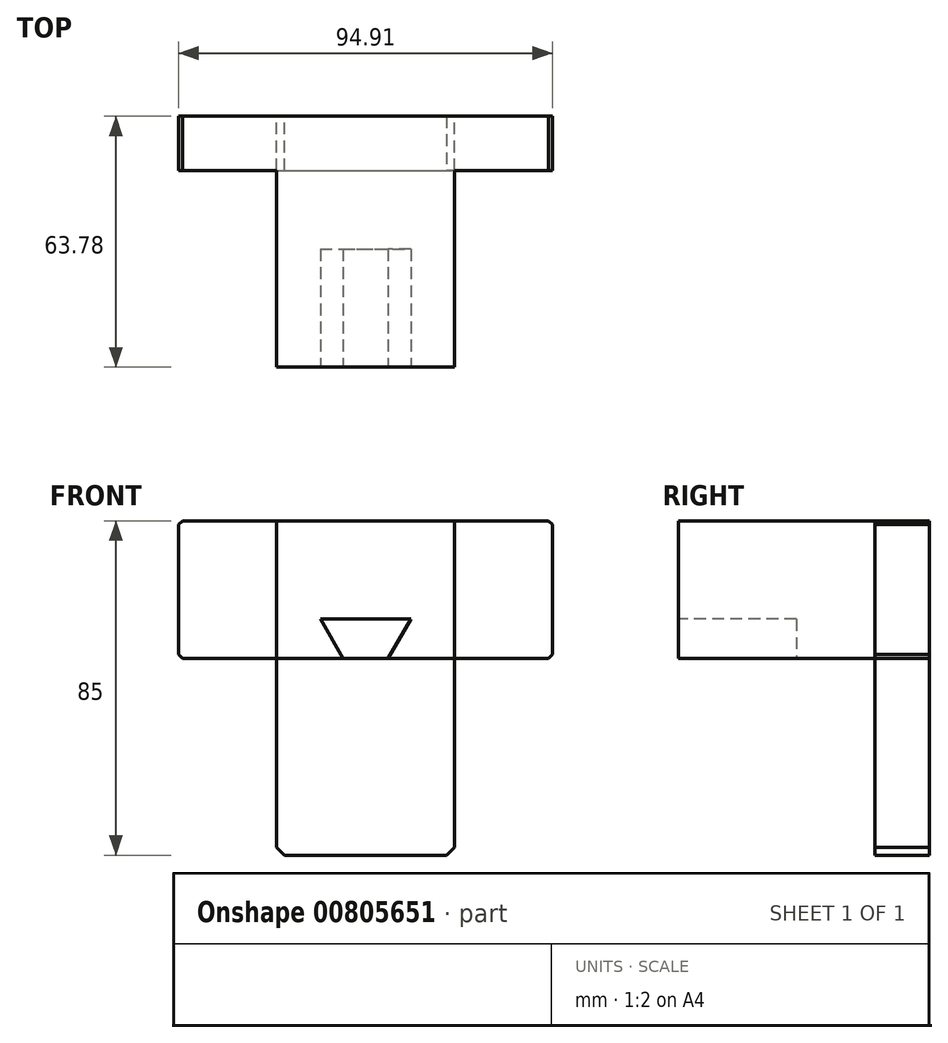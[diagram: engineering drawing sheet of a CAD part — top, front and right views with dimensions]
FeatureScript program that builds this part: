
annotation { "Feature Type Name" : "Feature", "Feature Type Description" : "" }
export const myFeature = defineFeature(function(context is Context, id is Id, definition is map)
    precondition{}
    {
        {
            var Q0;
            Q0=qCreatedBy(makeId("Front.planeOp"),FACE);
            var sketch = newSketch(context, id + "F0", { "sketchPlane" : qUnion([Q0])});
            skLineSegment(sketch, "E0.bottom", {"start": v(-47.93, 7.07) * mm, "end": v(46.98, 7.07) * mm});
            skLineSegment(sketch, "E0.top", {"start": v(-47.93, -27.93) * mm, "end": v(46.98, -27.93) * mm});
            skLineSegment(sketch, "E0.left", {"start": v(-47.93, 7.07) * mm, "end": v(-47.93, -27.93) * mm});
            skLineSegment(sketch, "E0.right", {"start": v(46.98, 7.07) * mm, "end": v(46.98, -27.93) * mm});
            skSolve(sketch);
        }
        {
            var Q0;
            Q0=makeQuery(id+"F0.imprint","IMPRINT",FACE,{"disambiguationData":[TD([[makeQuery(id+"F0.imprint","IMPRINT",EDGE,{"derivedFrom":sQuery(id+"F0.wireOp",EDGE,"E0.bottom")}),-1.0]])]});
            extrude(context, id + "F1", {"entities" : qUnion([Q0]), "depth" : 13.78 * mm, "offsetDistance" : 25 * mm});
        }
        {
            var Q0;
            Q0=makeQuery(id+"F1.opExtrude","SWEPT_EDGE",EDGE,{"disambiguationData":[OSD([sQuery(id+"F0.wireOp",EDGE,"E0.top"),sQuery(id+"F0.wireOp",EDGE,"E0.left")])]});
            var Q1;
            Q1=makeQuery(id+"F1.opExtrude","SWEPT_EDGE",EDGE,{"disambiguationData":[OSD([sQuery(id+"F0.wireOp",EDGE,"E0.top"),sQuery(id+"F0.wireOp",EDGE,"E0.right")])]});
            var Q2;
            Q2=makeQuery(id+"F1.opExtrude","SWEPT_EDGE",EDGE,{"disambiguationData":[OSD([sQuery(id+"F0.wireOp",EDGE,"E0.bottom"),sQuery(id+"F0.wireOp",EDGE,"E0.right")])]});
            var Q3;
            Q3=makeQuery(id+"F1.opExtrude","SWEPT_EDGE",EDGE,{"disambiguationData":[OSD([sQuery(id+"F0.wireOp",EDGE,"E0.bottom"),sQuery(id+"F0.wireOp",EDGE,"E0.left")])]});
            chamfer(context, id + "F2", {"entities" : qUnion([Q0, Q1, Q2, Q3]), "width" : 1 * mm, "tangentPropagation" : true});
        }
        {
            var Q0;
            Q0=makeQuery(id+"F1.opExtrude","CAP_FACE",FACE,{"disambiguationData":[OSD([sQuery(id+"F0.wireOp",EDGE,"E0.bottom"),sQuery(id+"F0.wireOp",EDGE,"E0.top"),sQuery(id+"F0.wireOp",EDGE,"E0.left"),sQuery(id+"F0.wireOp",EDGE,"E0.right")])],"isStart":false});
            var sketch = newSketch(context, id + "F3", { "sketchPlane" : qUnion([Q0])});
            skLineSegment(sketch, "E1.bottom", {"start": v(-23.06, 7.07) * mm, "end": v(22.1, 7.07) * mm});
            skLineSegment(sketch, "E1.top", {"start": v(-23.06, -27.93) * mm, "end": v(22.1, -27.93) * mm});
            skLineSegment(sketch, "E1.left", {"start": v(-23.06, 7.07) * mm, "end": v(-23.06, -27.93) * mm});
            skLineSegment(sketch, "E1.right", {"start": v(22.1, 7.07) * mm, "end": v(22.1, -27.93) * mm});
            skSolve(sketch);
        }
        {
            var Q0;
            Q0=makeQuery(id+"F3.imprint","IMPRINT",FACE,{"disambiguationData":[TD([[makeQuery(id+"F3.imprint","IMPRINT",EDGE,{"derivedFrom":sQuery(id+"F3.wireOp",EDGE,"E1.bottom")}),-1.0]])]});
            extrude(context, id + "F4", {"entities" : qUnion([Q0]), "operationType" : NewBodyOperationType.ADD, "depth" : 50 * mm, "offsetDistance" : 25 * mm});
        }
        {
            var Q0;
            Q0=makeQuery(id+"F4.boolean.opBoolean","MERGE",FACE,{"derivedFrom":[makeQuery(id+"F1.opExtrude","SWEPT_FACE",FACE,{"disambiguationData":[OSD([sQuery(id+"F0.wireOp",EDGE,"E0.top")])]}),makeQuery(id+"F4.opExtrude","SWEPT_FACE",FACE,{"disambiguationData":[OSD([sQuery(id+"F3.wireOp",EDGE,"E1.top")])]})]});
            var sketch = newSketch(context, id + "F5", { "sketchPlane" : qUnion([Q0])});
            skLineSegment(sketch, "E2.bottom", {"start": v(-23.06, 13.78) * mm, "end": v(22.1, 13.78) * mm});
            skLineSegment(sketch, "E2.top", {"start": v(-23.06, 0) * mm, "end": v(22.1, 0) * mm});
            skLineSegment(sketch, "E2.left", {"start": v(-23.06, 13.78) * mm, "end": v(-23.06, 0) * mm});
            skLineSegment(sketch, "E2.right", {"start": v(22.1, 13.78) * mm, "end": v(22.1, 0) * mm});
            skSolve(sketch);
        }
        {
            var Q0;
            Q0=makeQuery(id+"F5.imprint","IMPRINT",FACE,{"disambiguationData":[TD([[makeQuery(id+"F5.imprint","IMPRINT",EDGE,{"derivedFrom":sQuery(id+"F5.wireOp",EDGE,"E2.bottom")}),-1.0]])]});
            extrude(context, id + "F6", {"entities" : qUnion([Q0]), "operationType" : NewBodyOperationType.ADD, "depth" : 50 * mm, "offsetDistance" : 25 * mm});
        }
        {
            var Q0;
            Q0=makeQuery(id+"F4.opExtrude","CAP_FACE",FACE,{"disambiguationData":[OSD([sQuery(id+"F3.wireOp",EDGE,"E1.bottom"),sQuery(id+"F3.wireOp",EDGE,"E1.top"),sQuery(id+"F3.wireOp",EDGE,"E1.left"),sQuery(id+"F3.wireOp",EDGE,"E1.right")])],"isStart":false});
            var sketch = newSketch(context, id + "F7", { "sketchPlane" : qUnion([Q0])});
            skLineSegment(sketch, "E3.bottom", {"start": v(-11.98, -17.93) * mm, "end": v(11.02, -17.93) * mm});
            skLineSegment(sketch, "E3.top", {"start": v(-6.2, -27.93) * mm, "end": v(5.25, -27.93) * mm});
            skLineSegment(sketch, "E4", {"start": v(-11.98, -17.93) * mm, "end": v(-6.2, -27.93) * mm});
            skLineSegment(sketch, "E5", {"start": v(11.02, -17.93) * mm, "end": v(5.25, -27.93) * mm});
            skSolve(sketch);
        }
        {
            var Q0;
            Q0=makeQuery(id+"F7.imprint","IMPRINT",FACE,{"disambiguationData":[TD([[makeQuery(id+"F7.imprint","IMPRINT",EDGE,{"derivedFrom":sQuery(id+"F7.wireOp",EDGE,"E3.bottom")}),-1.0]])]});
            extrude(context, id + "F8", {"entities" : qUnion([Q0]), "operationType" : NewBodyOperationType.REMOVE, "oppositeDirection" : true, "depth" : 30 * mm, "offsetDistance" : 25 * mm});
        }
        {
            var Q0;
            Q0=makeQuery(id+"F6.opExtrude","CAP_EDGE",EDGE,{"disambiguationData":[OSD([sQuery(id+"F5.wireOp",EDGE,"E2.left")])],"isStart":false});
            var Q1;
            Q1=makeQuery(id+"F6.opExtrude","CAP_EDGE",EDGE,{"disambiguationData":[OSD([sQuery(id+"F5.wireOp",EDGE,"E2.right")])],"isStart":false});
            chamfer(context, id + "F9", {"entities" : qUnion([Q0, Q1]), "width" : 2 * mm, "tangentPropagation" : true});
        }
    });
